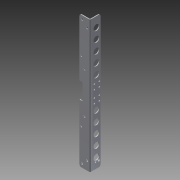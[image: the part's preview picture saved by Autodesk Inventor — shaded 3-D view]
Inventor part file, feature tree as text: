
AUTODESK INVENTOR PART (.ipt)
format: ipt  version: 2014 SP1 (Build 180222100, 222)  size: 340,992 bytes
history: native  units: in
note: dims shown in document units (in); Inventor stores cm internally (conversion verified against a paired STEP export)
features: other x5, reference x5, sketch x4, sheet_metal_op x2, chamfer x1
ambient origin geometry x8: Origin, YZ Plane, XZ Plane, XY Plane, X Axis, Y Axis, Z Axis, Center Point
bodies: Solid1 (feature_tree)
feature tree (17):
  sketch  "Sketch1"  dims[d0=20.0in]
  sheet_metal_op  "Face1"
  sheet_metal_op  "Fold1"
  chamfer  "Corner Round1"
  other  "Plate1"
  sketch  "Sketch2"  dims[d1=3.0in]
  reference  "Reference1"
  reference  "Reference2"
  sketch  "Sketch3"  dims[d2=1.5in]
  reference  "Reference3"
  reference  "Reference4"
  reference  "Reference5"
  sketch  "Sketch4"  dims[d3=0.25in d4=0.01in d5=0.25in d6=11.811in d8=0.6638in d9=0.3937in d11=1.0in d13=0.125in d14=0.125in d15=0.0625in d16=0.25in d17=0.125in d18=90.0deg d19=0.05in d20=0.313in d22=0.75in d23=0.313in d24=0.313in d25=0.375in d26=0.75in d27=0.75in d28=0.55in d29=0.125in d30=0.0in d31=6.2008in d32=0.25in d33=0.5in d34=0.875in d35=0.875in d36=1.5in d37=4.7244in d39=1.5455in d40=0.3937in d42=1.0in d44=0.125in d45=0.0in d46=0.266in d47=0.266in d48=0.25in d49=9.25in d50=0.125in d51=0.0in]
  other  "Cut1"
  other  "Cut2"
  other  "Cut3"
  other  "Definition1"
